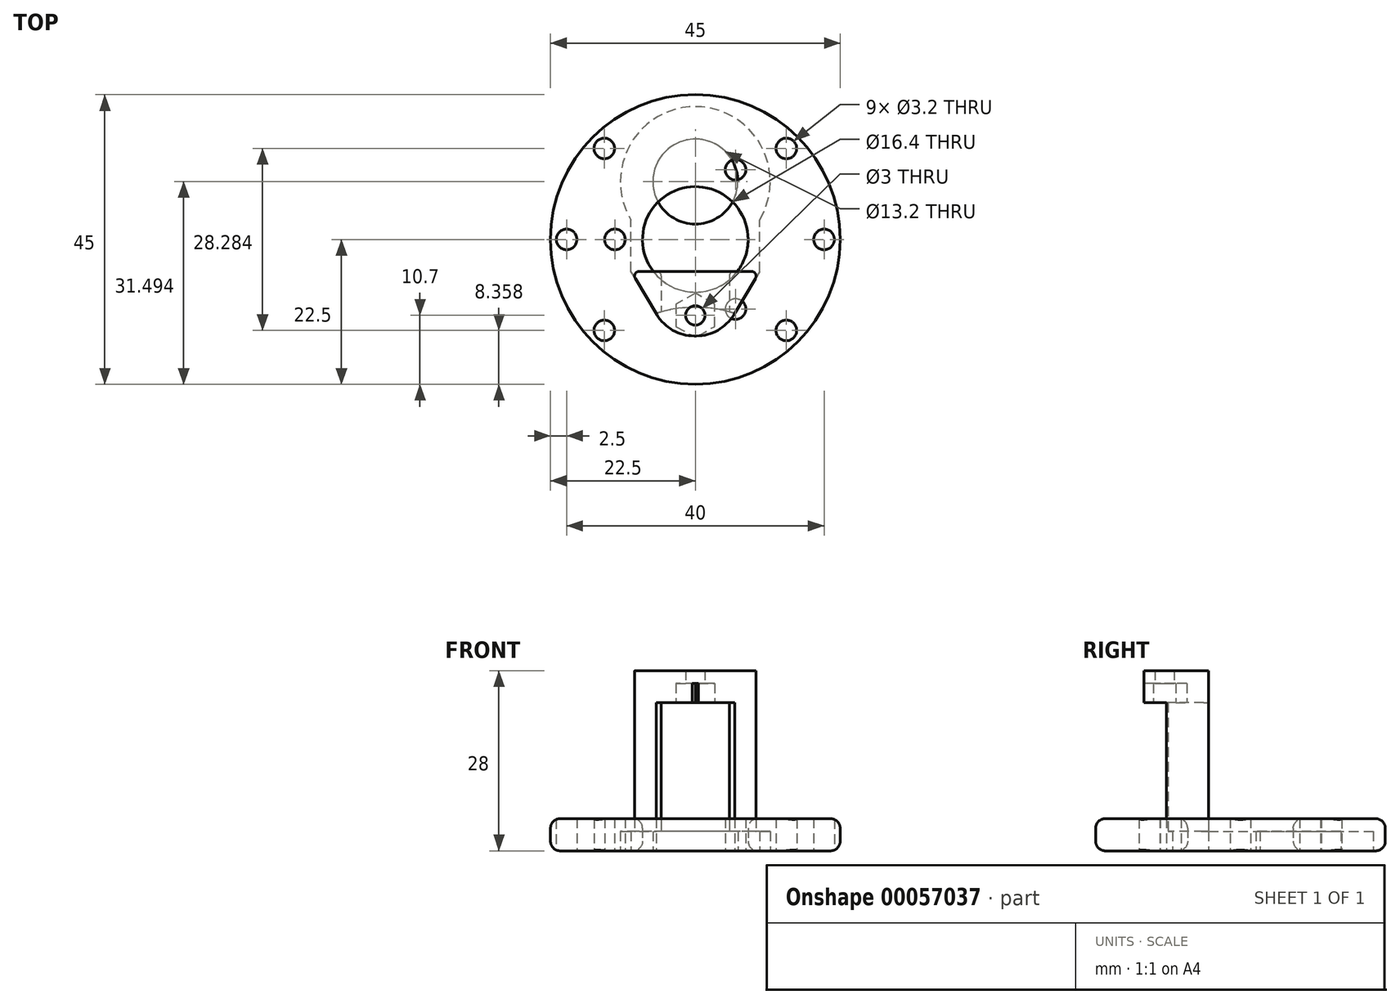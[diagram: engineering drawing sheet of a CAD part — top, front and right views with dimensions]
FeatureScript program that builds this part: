
annotation { "Feature Type Name" : "Feature", "Feature Type Description" : "" }
export const myFeature = defineFeature(function(context is Context, id is Id, definition is map)
    precondition{}
    {
        {
            var Q0;
            Q0=qCreatedBy(makeId("Top.planeOp"),FACE);
            var sketch = newSketch(context, id + "F0", { "sketchPlane" : qUnion([Q0])});
            skArc(sketch, "E0", {"start": v(10, 3.05) * mm, "mid": v(0, 20.63) * mm, "end": v(-10, 3.05) * mm});
            skLineSegment(sketch, "E1", {"start": v(-6.09, -11.5) * mm, "end": v(-10, -4.95) * mm});
            skLineSegment(sketch, "E2", {"start": v(10, -4.95) * mm, "end": v(6.09, -11.5) * mm});
            skLineSegment(sketch, "E3", {"start": v(-10, -4.95) * mm, "end": v(-10, 3.05) * mm});
            skLineSegment(sketch, "E4", {"start": v(10, -4.95) * mm, "end": v(10, 3.05) * mm});
            skCircle(sketch, "E5", {"center": v(0, 9) * mm, "radius": 6.6 * mm});
            skPoint(sketch, "E6", {"position": v(0, -15) * mm});
            skPoint(sketch, "E7.visualSharp", {"position": v(-4, -15) * mm});
            skPoint(sketch, "E8.visualSharp", {"position": v(4, -15) * mm});
            skArc(sketch, "E9", {"start": v(6.09, -11.5) * mm, "mid": v(0, -10.55) * mm, "end": v(-6.09, -11.5) * mm});
            skSolve(sketch);
        }
        {
            var Q0;
            Q0=makeQuery(id+"F0.imprint","IMPRINT",FACE,{"disambiguationData":[TD([[makeQuery(id+"F0.imprint","IMPRINT",EDGE,{"derivedFrom":sQuery(id+"F0.wireOp",EDGE,"E0")}),1.0]])]});
            extrude(context, id + "F1", {"entities" : qUnion([Q0]), "depth" : 3 * mm});
        }
        {
            var Q0;
            Q0=makeQuery(id+"F1.opExtrude","CAP_FACE",FACE,{"disambiguationData":[OSD([sQuery(id+"F0.wireOp",EDGE,"E0"),sQuery(id+"F0.wireOp",EDGE,"E1"),sQuery(id+"F0.wireOp",EDGE,"E2"),sQuery(id+"F0.wireOp",EDGE,"1279786a-ca67-4dae-8dfa-a27e434e7692"),sQuery(id+"F0.wireOp",EDGE,"E3"),sQuery(id+"F0.wireOp",EDGE,"E4"),sQuery(id+"F0.wireOp",EDGE,"E5")])],"isStart":false});
            var sketch = newSketch(context, id + "F2", { "sketchPlane" : qUnion([Q0])});
            skLineSegment(sketch, "E10", {"start": v(-8.7, -4.95) * mm, "end": v(-6.02, -4.95) * mm});
            skLineSegment(sketch, "E11", {"start": v(-5.28, -5.7) * mm, "end": v(-5.28, -12.14) * mm});
            skLineSegment(sketch, "E12", {"start": v(-5.65, -12.24) * mm, "end": v(-9.33, -6.07) * mm});
            skLineSegment(sketch, "E13.MirrorCS", {"start": v(8.7, -4.95) * mm, "end": v(6.02, -4.95) * mm});
            skLineSegment(sketch, "E14.MirrorCS", {"start": v(5.65, -12.24) * mm, "end": v(9.33, -6.07) * mm});
            skLineSegment(sketch, "E15.MirrorCS", {"start": v(5.28, -5.7) * mm, "end": v(5.28, -12.14) * mm});
            skPoint(sketch, "E16.visualSharp", {"position": v(-5.28, -4.95) * mm});
            skArc(sketch, "E16.filletArc", {"start": v(-5.28, -5.7) * mm, "mid": v(-5.5, -5.17) * mm, "end": v(-6.02, -4.95) * mm});
            skPoint(sketch, "E17.visualSharp", {"position": v(-10, -4.95) * mm});
            skArc(sketch, "E17.filletArc", {"start": v(-8.7, -4.95) * mm, "mid": v(-9.34, -5.33) * mm, "end": v(-9.33, -6.07) * mm});
            skPoint(sketch, "E18.visualSharp", {"position": v(-5.28, -12.86) * mm});
            skArc(sketch, "E18.filletArc", {"start": v(-5.65, -12.24) * mm, "mid": v(-5.42, -12.33) * mm, "end": v(-5.28, -12.14) * mm});
            skPoint(sketch, "E19.visualSharp", {"position": v(5.28, -4.95) * mm});
            skArc(sketch, "E19.filletArc", {"start": v(6.02, -4.95) * mm, "mid": v(5.5, -5.17) * mm, "end": v(5.28, -5.7) * mm});
            skPoint(sketch, "E20.visualSharp", {"position": v(10, -4.95) * mm});
            skArc(sketch, "E20.filletArc", {"start": v(9.33, -6.07) * mm, "mid": v(9.34, -5.33) * mm, "end": v(8.7, -4.95) * mm});
            skPoint(sketch, "E21.visualSharp", {"position": v(5.28, -12.86) * mm});
            skArc(sketch, "E21.filletArc", {"start": v(5.28, -12.14) * mm, "mid": v(5.42, -12.33) * mm, "end": v(5.65, -12.24) * mm});
            skSolve(sketch);
        }
        {
            var Q0;
            Q0=makeQuery(id+"F2.imprint","IMPRINT",FACE,{"disambiguationData":[TD([[makeQuery(id+"F2.imprint","IMPRINT",EDGE,{"derivedFrom":sQuery(id+"F2.wireOp",EDGE,"E10")}),-1.0]])]});
            var Q1;
            Q1=makeQuery(id+"F2.imprint","IMPRINT",FACE,{"disambiguationData":[TD([[makeQuery(id+"F2.imprint","IMPRINT",EDGE,{"derivedFrom":sQuery(id+"F2.wireOp",EDGE,"E13.MirrorCS")}),1.0]])]});
            extrude(context, id + "F3", {"entities" : qUnion([Q0, Q1]), "operationType" : NewBodyOperationType.ADD, "depth" : 20 * mm});
        }
        {
            var Q0;
            Q0=makeQuery(id+"F3.opExtrude","CAP_FACE",FACE,{"disambiguationData":[OSD([sQuery(id+"F2.wireOp",EDGE,"E10"),sQuery(id+"F2.wireOp",EDGE,"E11"),sQuery(id+"F2.wireOp",EDGE,"E12"),sQuery(id+"F2.wireOp",EDGE,"E16.filletArc"),sQuery(id+"F2.wireOp",EDGE,"E17.filletArc"),sQuery(id+"F2.wireOp",EDGE,"E18.filletArc")])],"isStart":false});
            var sketch = newSketch(context, id + "F4", { "sketchPlane" : qUnion([Q0])});
            skLineSegment(sketch, "E22", {"start": v(-8.7, -4.95) * mm, "end": v(8.7, -4.95) * mm});
            skLineSegment(sketch, "E23", {"start": v(9.33, -6.07) * mm, "end": v(5.97, -11.7) * mm});
            skLineSegment(sketch, "E24", {"start": v(-5.97, -11.7) * mm, "end": v(-9.33, -6.07) * mm});
            skCircle(sketch, "E25", {"center": v(0, -11.8) * mm, "radius": 1.5 * mm});
            skPoint(sketch, "E26.visualSharp", {"position": v(-10, -4.95) * mm});
            skArc(sketch, "E26.filletArc", {"start": v(-8.7, -4.95) * mm, "mid": v(-9.34, -5.33) * mm, "end": v(-9.33, -6.07) * mm});
            skPoint(sketch, "E27.visualSharp", {"position": v(10, -4.95) * mm});
            skArc(sketch, "E27.filletArc", {"start": v(9.33, -6.07) * mm, "mid": v(9.34, -5.33) * mm, "end": v(8.7, -4.95) * mm});
            skLineSegment(sketch, "E28", {"start": v(-0.15, -15) * mm, "end": v(0.15, -15) * mm});
            skPoint(sketch, "E29.visualSharp", {"position": v(-4, -15) * mm});
            skArc(sketch, "E29.filletArc", {"start": v(-5.97, -11.7) * mm, "mid": v(-3.5, -14.12) * mm, "end": v(-0.15, -15) * mm});
            skPoint(sketch, "E30.visualSharp", {"position": v(4, -15) * mm});
            skArc(sketch, "E30.filletArc", {"start": v(0.15, -15) * mm, "mid": v(3.5, -14.12) * mm, "end": v(5.97, -11.7) * mm});
            skSolve(sketch);
        }
        {
            var Q0;
            Q0=makeQuery(id+"F4.imprint","IMPRINT",FACE,{"disambiguationData":[TD([[makeQuery(id+"F4.imprint","IMPRINT",EDGE,{"derivedFrom":sQuery(id+"F4.wireOp",EDGE,"E23")}),-1.0]])]});
            var Q1;
            {var subQ1=sQuery(id+"F4.wireOp",EDGE,"E24");Q1=makeQuery(id+"F4.imprint","IMPRINT",FACE,{"disambiguationData":[TD([[makeQuery(id+"F4.imprint","IMPRINT",EDGE,{"derivedFrom":subQ1}),-1.0]])]});}
            extrude(context, id + "F5", {"entities" : qUnion([Q0, Q1]), "operationType" : NewBodyOperationType.ADD, "depth" : 5 * mm});
        }
        {
            var Q0;
            Q0=makeQuery(id+"F5.opExtrude","CAP_FACE",FACE,{"disambiguationData":[OSD([sQuery(id+"F4.wireOp",EDGE,"E22"),sQuery(id+"F4.wireOp",EDGE,"E23"),sQuery(id+"F4.wireOp",EDGE,"E24"),sQuery(id+"F4.wireOp",EDGE,"E25"),sQuery(id+"F4.wireOp",EDGE,"E26.filletArc"),sQuery(id+"F4.wireOp",EDGE,"E27.filletArc"),sQuery(id+"F4.wireOp",EDGE,"E28"),sQuery(id+"F4.wireOp",EDGE,"E29.filletArc"),sQuery(id+"F4.wireOp",EDGE,"E30.filletArc")])],"isStart":true});
            var sketch = newSketch(context, id + "F6", { "sketchPlane" : qUnion([Q0])});
            skCircle(sketch, "E31.cCircle", {"center": v(0, 11.8) * mm, "radius": 3 * mm, "construction": true});
            skLineSegment(sketch, "E31.0", {"start": v(-3, 13.53) * mm, "end": v(0, 15.26) * mm});
            skLineSegment(sketch, "E31.1", {"start": v(0, 15.26) * mm, "end": v(3, 13.53) * mm});
            skLineSegment(sketch, "E31.2", {"start": v(3, 13.53) * mm, "end": v(3, 10.07) * mm});
            skLineSegment(sketch, "E31.3", {"start": v(3, 10.07) * mm, "end": v(0, 8.34) * mm});
            skLineSegment(sketch, "E31.4", {"start": v(0, 8.34) * mm, "end": v(-3, 10.07) * mm});
            skLineSegment(sketch, "E31.5", {"start": v(-3, 10.07) * mm, "end": v(-3, 13.53) * mm});
            skPoint(sketch, "E31.0.midPoint", {"position": v(-1.5, 14.4) * mm});
            skSolve(sketch);
        }
        {
            var Q0;
            {var subQ4=sQuery(id+"F6.wireOp",EDGE,"E31.2");Q0=makeQuery(id+"F6.imprint","IMPRINT",FACE,{"disambiguationData":[TD([[makeQuery(id+"F6.imprint","IMPRINT",EDGE,{"derivedFrom":subQ4}),-1.0]])]});}
            extrude(context, id + "F7", {"entities" : qUnion([Q0]), "operationType" : NewBodyOperationType.REMOVE, "oppositeDirection" : true, "depth" : 3 * mm});
        }
        {
            var Q0;
            Q0=qCreatedBy(makeId("Top.planeOp"),FACE);
            var sketch = newSketch(context, id + "F8", { "sketchPlane" : qUnion([Q0])});
            skCircle(sketch, "E32", {"center": v(0, 0) * mm, "radius": 22.5 * mm});
            skCircle(sketch, "E33", {"center": v(0, 0) * mm, "radius": 8.2 * mm});
            skCircle(sketch, "E34", {"center": v(6.25, 10.83) * mm, "radius": 1.6 * mm});
            skCircle(sketch, "E35", {"center": v(6.25, -10.83) * mm, "radius": 1.6 * mm});
            skCircle(sketch, "E36", {"center": v(-12.5, 0) * mm, "radius": 1.6 * mm});
            skLineSegment(sketch, "E37", {"start": v(0, 0) * mm, "end": v(23.13, 40.06) * mm, "construction": true});
            skLineSegment(sketch, "E38", {"start": v(0, 0) * mm, "end": v(-38.78, 0) * mm, "construction": true});
            skLineSegment(sketch, "E39", {"start": v(0, 0) * mm, "end": v(15.97, -27.67) * mm, "construction": true});
            skCircle(sketch, "E40", {"center": v(0, 0) * mm, "radius": 12.5 * mm, "construction": true});
            skCircle(sketch, "E41", {"center": v(0, 0) * mm, "radius": 20 * mm, "construction": true});
            skLineSegment(sketch, "E42", {"start": v(0, 0) * mm, "end": v(24.24, 24.24) * mm, "construction": true});
            skLineSegment(sketch, "E43", {"start": v(0, 0) * mm, "end": v(23.64, -23.64) * mm, "construction": true});
            skCircle(sketch, "E44", {"center": v(14.14, 14.14) * mm, "radius": 1.6 * mm});
            skCircle(sketch, "E45", {"center": v(20, 0) * mm, "radius": 1.6 * mm});
            skCircle(sketch, "E46", {"center": v(14.14, -14.14) * mm, "radius": 1.6 * mm});
            skCircle(sketch, "E47.MirrorC", {"center": v(-14.14, 14.14) * mm, "radius": 1.6 * mm});
            skCircle(sketch, "E48.MirrorC", {"center": v(-20, 0) * mm, "radius": 1.6 * mm});
            skCircle(sketch, "E49.MirrorC", {"center": v(-14.14, -14.14) * mm, "radius": 1.6 * mm});
            skSolve(sketch);
        }
        {
            var Q0;
            Q0=makeQuery(id+"F8.imprint","IMPRINT",FACE,{"disambiguationData":[TD([[makeQuery(id+"F8.imprint","IMPRINT",EDGE,{"derivedFrom":sQuery(id+"F8.wireOp",EDGE,"E32")}),1.0]])]});
            extrude(context, id + "F9", {"entities" : qUnion([Q0]), "depth" : 5 * mm});
        }
        {
            var Q0;
            Q0=makeQuery(id+"F9.opExtrude","CAP_EDGE",EDGE,{"disambiguationData":[OSD([sQuery(id+"F8.wireOp",EDGE,"E32")])],"isStart":false});
            fillet(context, id + "F10", {"entities" : qUnion([Q0]), "radius" : 1.5 * mm, "tangentPropagation" : true, "allowEdgeOverflow" : false});
        }
        {
            var Q0;
            Q0=makeQuery(id+"F9.opExtrude","CAP_EDGE",EDGE,{"disambiguationData":[OSD([sQuery(id+"F8.wireOp",EDGE,"E32")])],"isStart":true});
            var Q1;
            Q1=makeQuery(id+"F9.opExtrude","CAP_EDGE",EDGE,{"disambiguationData":[OSD([sQuery(id+"F8.wireOp",EDGE,"E33")])],"isStart":true});
            var Q2;
            Q2=makeQuery(id+"F9.opExtrude","CAP_EDGE",EDGE,{"disambiguationData":[OSD([sQuery(id+"F8.wireOp",EDGE,"E33")])],"isStart":false});
            fillet(context, id + "F11", {"entities" : qUnion([Q0, Q1, Q2]), "radius" : 1.5 * mm, "tangentPropagation" : true, "allowEdgeOverflow" : false});
        }
    });
